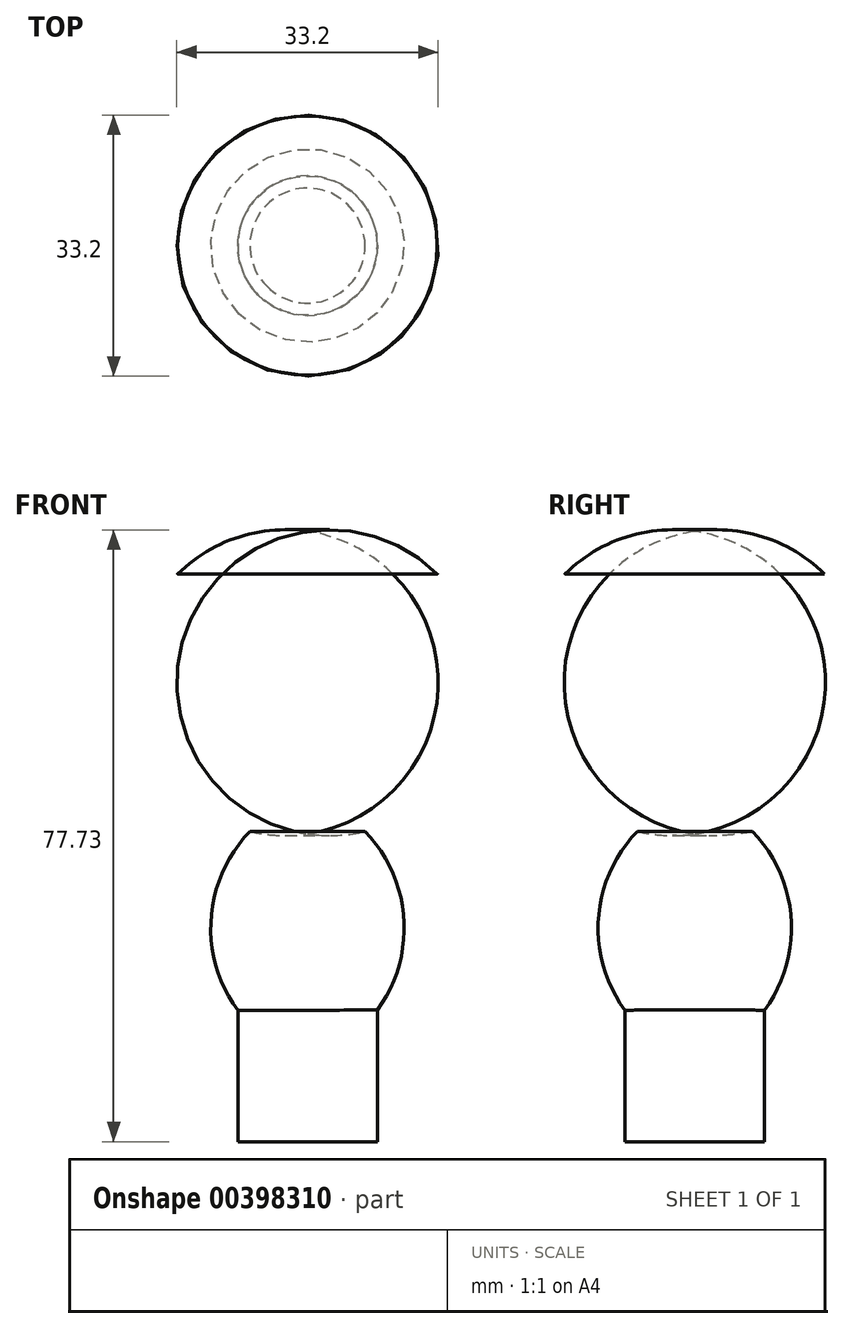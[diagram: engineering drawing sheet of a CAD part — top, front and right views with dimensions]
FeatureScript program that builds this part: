
annotation { "Feature Type Name" : "Feature", "Feature Type Description" : "" }
export const myFeature = defineFeature(function(context is Context, id is Id, definition is map)
    precondition{}
    {
        {
            var Q0;
            Q0=qCreatedBy(makeId("Front.planeOp"),FACE);
            var sketch = newSketch(context, id + "F0", { "sketchPlane" : qUnion([Q0])});
            skLineSegment(sketch, "E0", {"start": v(-89.97, 61.49) * mm, "end": v(-89.97, -69.72) * mm});
            skArc(sketch, "E1", {"start": v(-89.97, 18.15) * mm, "mid": v(-58.51, 39.82) * mm, "end": v(-89.97, 61.49) * mm});
            skArc(sketch, "E2", {"start": v(-89.97, -14.9) * mm, "mid": v(-67.72, 4.31) * mm, "end": v(-89.97, 23.53) * mm});
            skArc(sketch, "E3", {"start": v(-89.97, -43.66) * mm, "mid": v(-77.68, -26.86) * mm, "end": v(-89.97, -10.07) * mm});
            skSolve(sketch);
        }
        {
            var Q0;
            Q0 = qSketchRegion(id + "F0", true);
            var Q1;
            Q1=sQuery(id+"F0.wireOp",EDGE,"E0");
            revolve(context, id + "F1", {"entities" : qUnion([Q0]), "axis" : qUnion([Q1]), "revolveType" : RevolveType.FULL});
        }
        {
            var Q0;
            Q0=qCreatedBy(makeId("Front.planeOp"),FACE);
            var sketch = newSketch(context, id + "F2", { "sketchPlane" : qUnion([Q0])});
            skLineSegment(sketch, "E4", {"start": v(-103.92, -37.26) * mm, "end": v(-76, -37.26) * mm});
            skLineSegment(sketch, "E5", {"start": v(-89.95, -37.26) * mm, "end": v(-89.95, -54) * mm});
            skLineSegment(sketch, "E6", {"start": v(-89.95, -54) * mm, "end": v(-81.1, -54) * mm});
            skLineSegment(sketch, "E7", {"start": v(-81.1, -54) * mm, "end": v(-81.1, -37.26) * mm});
            skSolve(sketch);
        }
        {
            var Q0;
            Q0 = qSketchRegion(id + "F2", true);
            var Q1;
            Q1=sQuery(id+"F2.wireOp",EDGE,"E5");
            revolve(context, id + "F3", {"operationType" : NewBodyOperationType.ADD, "entities" : qUnion([Q0]), "axis" : qUnion([Q1]), "revolveType" : RevolveType.FULL});
        }
    });
